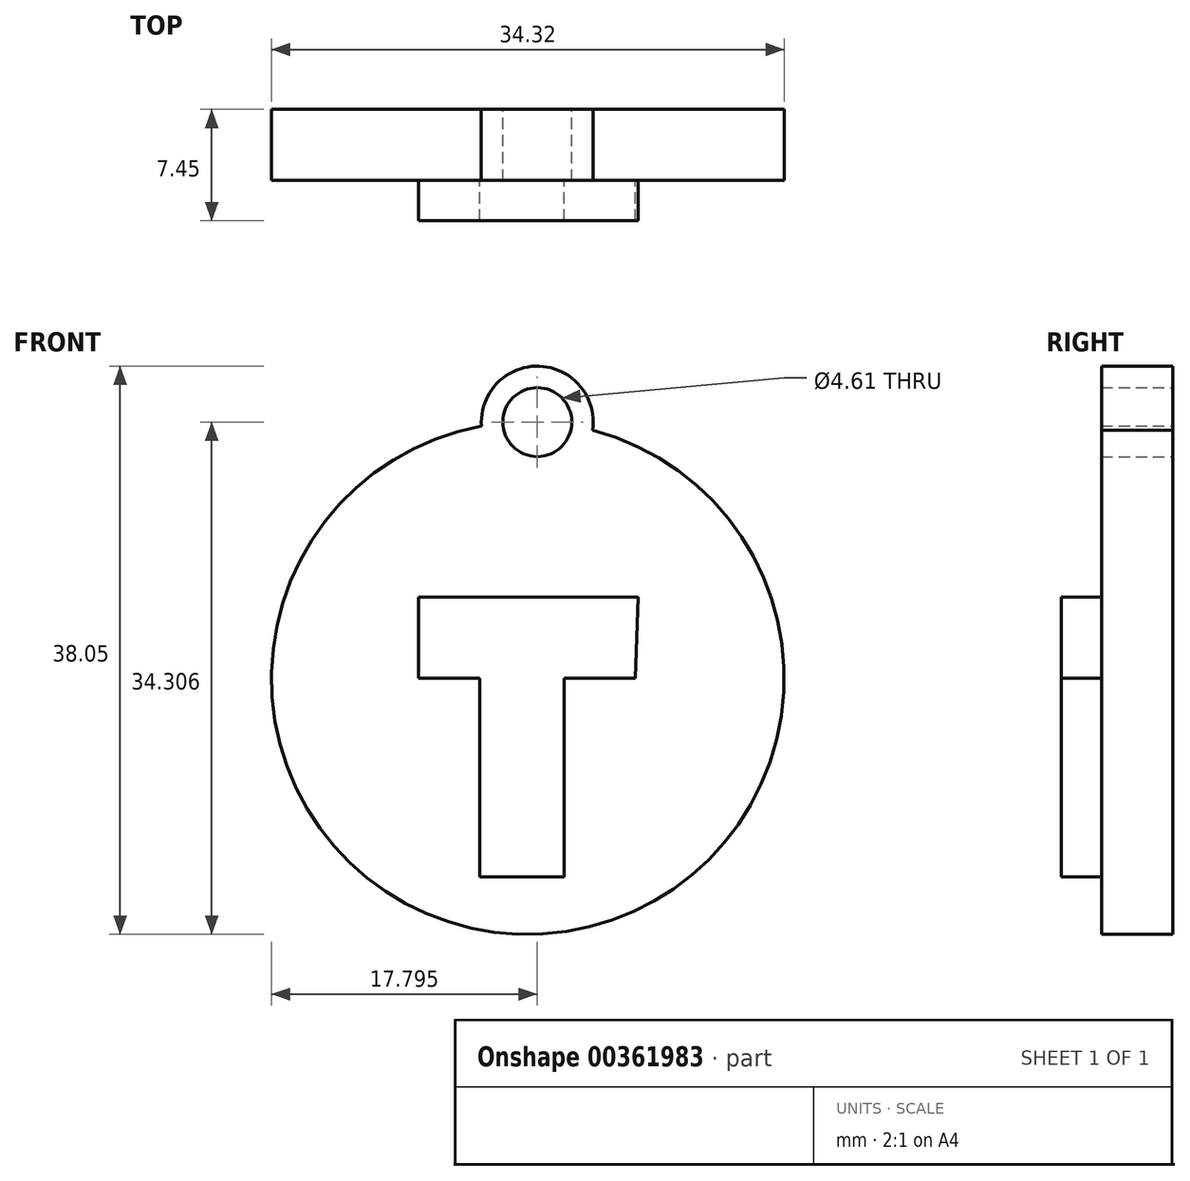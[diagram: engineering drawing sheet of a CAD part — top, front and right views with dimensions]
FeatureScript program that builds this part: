
annotation { "Feature Type Name" : "Feature", "Feature Type Description" : "" }
export const myFeature = defineFeature(function(context is Context, id is Id, definition is map)
    precondition{}
    {
        {
            var Q0;
            Q0=qCreatedBy(makeId("Front.planeOp"),FACE);
            var sketch = newSketch(context, id + "F0", { "sketchPlane" : qUnion([Q0])});
            skArc(sketch, "E0", {"start": v(4.34, 16.6) * mm, "mid": v(0.77, 20.89) * mm, "end": v(-3.1, 16.88) * mm});
            skArc(sketch, "E1.trimOffspring", {"start": v(-3.1, 16.88) * mm, "mid": v(-0.63, -17.15) * mm, "end": v(4.34, 16.6) * mm});
            skPoint(sketch, "E2.center.orphan", {"position": v(0, 20.84) * mm});
            skPoint(sketch, "E3.start.orphan", {"position": v(0, -12.7) * mm});
            skPoint(sketch, "E4.start.orphan", {"position": v(-7.7, 0) * mm});
            skCircle(sketch, "E5", {"center": v(0.63, 17.15) * mm, "radius": 2.3 * mm});
            skSolve(sketch);
        }
        {
            var Q0;
            Q0=makeQuery(id+"F0.imprint","IMPRINT",FACE,{"disambiguationData":[TD([[makeQuery(id+"F0.imprint","IMPRINT",EDGE,{"derivedFrom":sQuery(id+"F0.wireOp",EDGE,"E0")}),1.0]])]});
            extrude(context, id + "F1", {"entities" : qUnion([Q0]), "depth" : 4.76 * mm});
        }
        {
            var Q0;
            Q0=makeQuery(id+"F1.opExtrude","CAP_FACE",FACE,{"disambiguationData":[OSD([sQuery(id+"F0.wireOp",EDGE,"E0"),sQuery(id+"F0.wireOp",EDGE,"E1.trimOffspring"),sQuery(id+"F0.wireOp",EDGE,"E5")])],"isStart":false});
            var sketch = newSketch(context, id + "F2", { "sketchPlane" : qUnion([Q0])});
            skLineSegment(sketch, "E6", {"start": v(-7.33, 0) * mm, "end": v(6.36, 0) * mm});
            skPoint(sketch, "E7.end.orphan", {"position": v(0, -1.67) * mm});
            skLineSegment(sketch, "E8", {"start": v(-7.33, 0) * mm, "end": v(-7.33, 5.41) * mm});
            skPoint(sketch, "E9.end.orphan", {"position": v(7.2, 0) * mm});
            skLineSegment(sketch, "E10", {"start": v(-7.33, 5.41) * mm, "end": v(7.38, 5.41) * mm});
            skLineSegment(sketch, "E11", {"start": v(7.38, 5.41) * mm, "end": v(7.2, 0) * mm});
            skLineSegment(sketch, "E12", {"start": v(-3.23, 0) * mm, "end": v(-3.23, -13.3) * mm});
            skLineSegment(sketch, "E13", {"start": v(-3.23, -13.3) * mm, "end": v(2.44, -13.3) * mm});
            skLineSegment(sketch, "E14", {"start": v(2.44, 0) * mm, "end": v(2.44, -13.3) * mm});
            skLineSegment(sketch, "E15", {"start": v(7.2, 0) * mm, "end": v(6.36, 0) * mm});
            skSolve(sketch);
        }
        {
            var Q0;
            {var subQ0=sQuery(id+"F2.wireOp",EDGE,"E8");Q0=makeQuery(id+"F2.imprint","IMPRINT",FACE,{"disambiguationData":[TD([[makeQuery(id+"F2.imprint","IMPRINT",EDGE,{"derivedFrom":subQ0}),-1.0]])]});}
            var Q1;
            {var subQ0=sQuery(id+"F2.wireOp",EDGE,"E12");Q1=makeQuery(id+"F2.imprint","IMPRINT",FACE,{"disambiguationData":[TD([[makeQuery(id+"F2.imprint","IMPRINT",EDGE,{"derivedFrom":subQ0}),1.0]])]});}
            extrude(context, id + "F3", {"entities" : qUnion([Q0, Q1]), "operationType" : NewBodyOperationType.ADD, "depth" : 2.7 * mm});
        }
    });
